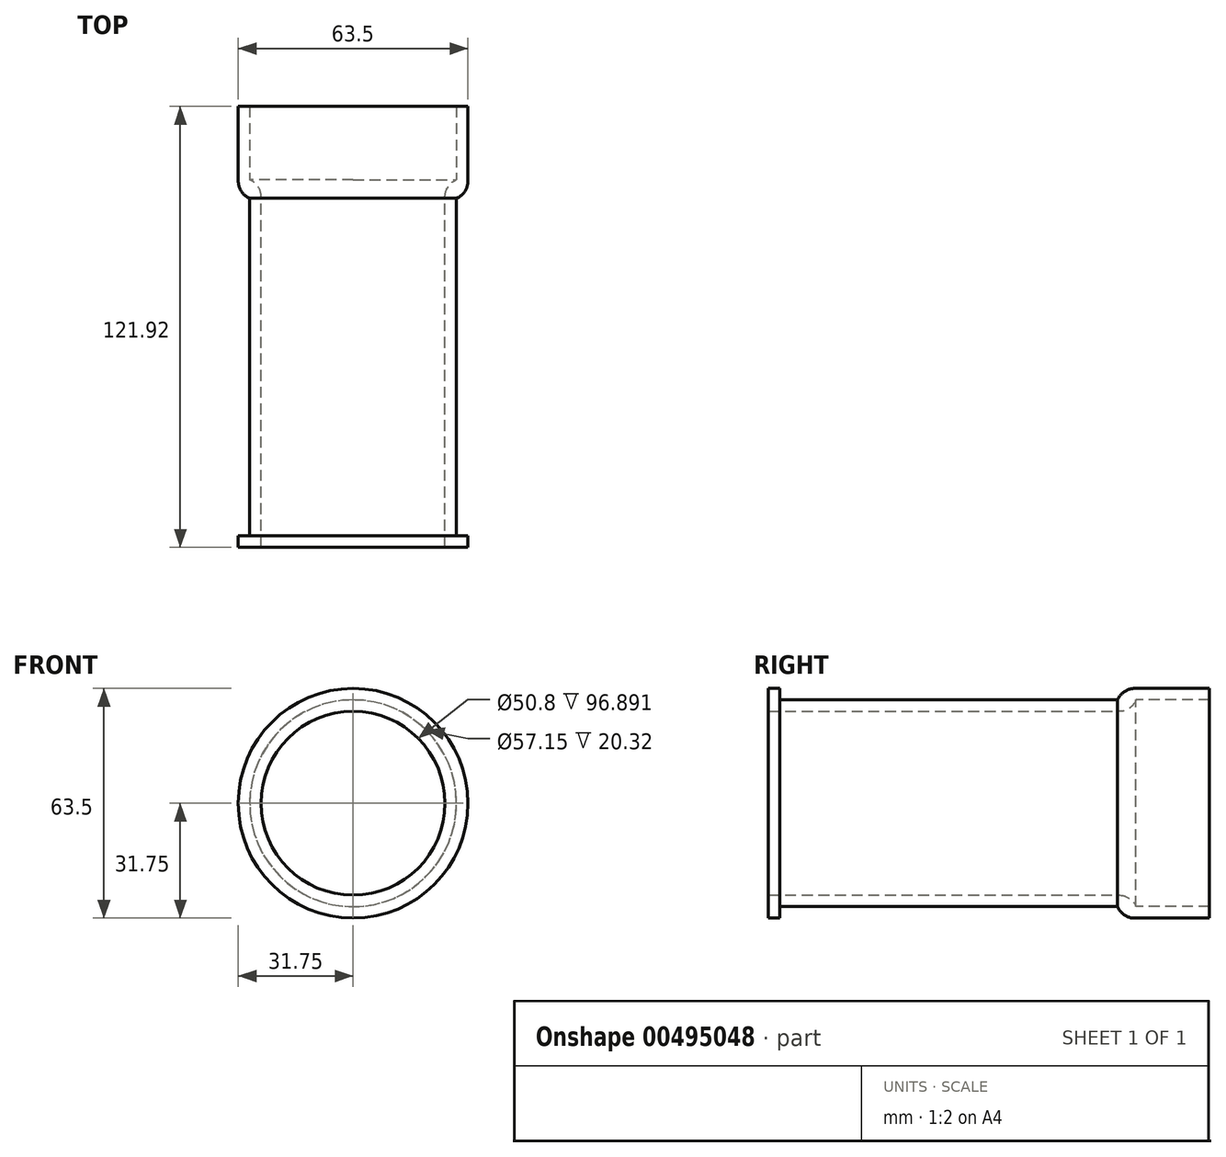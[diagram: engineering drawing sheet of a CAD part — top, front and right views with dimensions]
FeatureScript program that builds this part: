
annotation { "Feature Type Name" : "Feature", "Feature Type Description" : "" }
export const myFeature = defineFeature(function(context is Context, id is Id, definition is map)
    precondition{}
    {
        {
            var Q0;
            Q0=qCreatedBy(makeId("Front.planeOp"),FACE);
            var sketch = newSketch(context, id + "F0", { "sketchPlane" : qUnion([Q0])});
            skCircle(sketch, "E0", {"center": v(0, 0) * mm, "radius": 25.4 * mm});
            skCircle(sketch, "E1", {"center": v(0, 0) * mm, "radius": 28.58 * mm});
            skCircle(sketch, "E2", {"center": v(0, 0) * mm, "radius": 31.75 * mm});
            skSolve(sketch);
        }
        {
            var Q0;
            Q0=qCreatedBy(makeId("Right.planeOp"),FACE);
            var sketch = newSketch(context, id + "F1", { "sketchPlane" : qUnion([Q0])});
            skLineSegment(sketch, "E3", {"start": v(0, 0) * mm, "end": v(101.6, 0) * mm});
            skLineSegment(sketch, "E4", {"start": v(101.6, 0) * mm, "end": v(101.6, 28.58) * mm});
            skLineSegment(sketch, "E5", {"start": v(101.6, 28.58) * mm, "end": v(96.52, 28.58) * mm});
            skLineSegment(sketch, "E6", {"start": v(96.52, 28.57) * mm, "end": v(96.52, 31.75) * mm});
            skLineSegment(sketch, "E7", {"start": v(96.52, 31.75) * mm, "end": v(121.92, 31.75) * mm});
            skLineSegment(sketch, "E8", {"start": v(121.92, 31.75) * mm, "end": v(121.92, 28.58) * mm});
            skLineSegment(sketch, "E9", {"start": v(121.92, 28.58) * mm, "end": v(101.6, 28.58) * mm});
            skSolve(sketch);
        }
        {
            var Q0;
            Q0=makeQuery(id+"F0.imprint","IMPRINT",FACE,{"disambiguationData":[TD([[makeQuery(id+"F0.imprint","IMPRINT",EDGE,{"derivedFrom":sQuery(id+"F0.wireOp",EDGE,"E0")}),-1.0]])]});
            var Q1;
            Q1=sQuery(id+"F1.wireOp",EDGE,"E3");
            sweep(context, id + "F2", {"profiles" : qUnion([Q0]), "path" : qUnion([Q1])});
        }
        {
            var Q0;
            Q0=makeQuery(id+"F0.imprint","IMPRINT",FACE,{"disambiguationData":[TD([[makeQuery(id+"F0.imprint","IMPRINT",EDGE,{"derivedFrom":sQuery(id+"F0.wireOp",EDGE,"E1")}),-1.0]])]});
            extrude(context, id + "F3", {"entities" : qUnion([Q0]), "operationType" : NewBodyOperationType.ADD, "oppositeDirection" : true, "depth" : 3.17 * mm});
        }
        {
            var Q0;
            Q0=makeQuery(id+"F1.imprint","IMPRINT",FACE,{"disambiguationData":[TD([[makeQuery(id+"F1.imprint","IMPRINT",EDGE,{"derivedFrom":sQuery(id+"F1.wireOp",EDGE,"E5")}),-1.0]])]});
            var Q1;
            Q1=sQuery(id+"F1.wireOp",EDGE,"E3");
            revolve(context, id + "F4", {"operationType" : NewBodyOperationType.ADD, "entities" : qUnion([Q0]), "axis" : qUnion([Q1]), "revolveType" : RevolveType.FULL});
        }
        {
            var Q0;
            Q0=makeQuery(id+"F2.opSweep","CAP_EDGE",EDGE,{"disambiguationData":[OSD([sQuery(id+"F0.wireOp",EDGE,"E0"),sQuery(id+"F1.wireOp",VERTEX,"E3.end")])],"isStart":false});
            var Q1;
            Q1=makeQuery(id+"F4.opRevolve","SWEPT_EDGE",EDGE,{"disambiguationData":[OSD([sQuery(id+"F1.wireOp",EDGE,"E6"),sQuery(id+"F1.wireOp",EDGE,"E7")])]});
            fillet(context, id + "F5", {"entities" : qUnion([Q0, Q1]), "radius" : 5.08 * mm, "tangentPropagation" : true, "allowEdgeOverflow" : false});
        }
    });
